# Revit family: 303_R14X_
name_source: partatom
category: Pipe Accessories
revit_build: Autodesk Revit 2018 (Build: 20170223_1515(x64)
units: mm (PartAtom-declared; Revit-internal decimal feet)

## family parameters
Always vertical = Yes
Cut with Voids When Loaded = No
Part Type = Valve - Breaks Into
Round Connector Dimension = Use Diameter
Shared = No
Work Plane-Based = No

## types (5) — shared parameters
CAT0 = Yes
CAT1 = No
Description = Angle lockshild valve
L2D_Min = 3048 mm
Manufacturer = Giacomini
QmdConnectorList = 301;D;302;D1
RC = No
URL = http://www.giacomini.com
Z1 = 2 mm  [stored 0.00656168 ft]
Z2 = 15 mm  [stored 0.0492126 ft]
magiPartTypeId = 303
magiProductFamilyId = R14X*
zero-valued in all types: MC_Default_elevation

## per-type parameters (varying)
- R14X032: B1=8 mm  [stored 0.0262467 ft]; B4=9 mm  [stored 0.0295276 ft]; CenSd_K1_6=10 mm  [stored 0.0328084 ft]; CenSd_W2_6=12 mm  [stored 0.0393701 ft]; D=10 mm; D1=10 mm; G1=8 mm  [stored 0.0262467 ft]; G3=10 mm  [stored 0.0328084 ft]; H3=9 mm  [stored 0.0295276 ft]; H3__ve=-9 mm; J=19 mm  [stored 0.062336 ft]; J1=5 mm  [stored 0.0164042 ft]; J3=7 mm  [stored 0.0229659 ft]; K1=11 mm  [stored 0.0360892 ft]; KH=8 mm  [stored 0.0262467 ft]; KH__ve=-8 mm  [stored -0.0262467 ft]; L=38 mm; L2=49 mm; L2D=38 mm; L3=7 mm  [stored 0.0229659 ft]; L4=7 mm  [stored 0.0229659 ft]; L4__ve=-7 mm; L5=3 mm  [stored 0.00984252 ft]; L8=10 mm  [stored 0.0328084 ft]; L8__ve=-10 mm  [stored -0.0328084 ft]; M1=15 mm  [stored 0.0492126 ft]; M12=11 mm  [stored 0.0360892 ft]; M3=17 mm  [stored 0.0557743 ft]; M3__ve=-17 mm  [stored -0.0557743 ft]; R1=8 mm  [stored 0.0262467 ft]; RC1=Yes; RC2=Yes; RC4=No; SW1=Yes; SW2=No; W1=11 mm  [stored 0.0360892 ft]; W2=14 mm  [stored 0.0459318 ft]; W2D=10 mm  [stored 0.0328084 ft]; W3=9 mm  [stored 0.0295276 ft]; X1=17 mm  [stored 0.0557743 ft]; X11=35 mm; X4=5 mm  [stored 0.0164042 ft]; Z4=11 mm  [stored 0.0360892 ft]
- R14X036: B1=17 mm  [stored 0.0557743 ft]; B4=21 mm  [stored 0.0688976 ft]; CenSd_K1_6=21 mm  [stored 0.0688976 ft]; CenSd_W2_6=23 mm; D=32 mm; D1=32 mm; G1=19 mm  [stored 0.062336 ft]; G3=21 mm  [stored 0.0688976 ft]; H3=18 mm; H3__ve=-18 mm; J=34 mm; J1=27 mm; J3=29 mm; K1=25 mm  [stored 0.082021 ft]; KH=14 mm  [stored 0.0459318 ft]; KH__ve=-14 mm; L=61 mm; L2=79 mm; L2D=60 mm; L3=13 mm; L4=13 mm; L4__ve=-13 mm; L5=6 mm  [stored 0.019685 ft]; L8=19 mm  [stored 0.062336 ft]; L8__ve=-19 mm  [stored -0.062336 ft]; M1=23 mm; M12=17 mm  [stored 0.0557743 ft]; M3=25 mm  [stored 0.082021 ft]; M3__ve=-25 mm; R1=19 mm  [stored 0.062336 ft]; RC1=No; RC2=No; RC4=Yes; SW1=No; SW2=Yes; W1=21 mm  [stored 0.0688976 ft]; W2=27 mm; W2D=32 mm; W3=19 mm  [stored 0.062336 ft]; X1=25 mm  [stored 0.082021 ft]; X11=54 mm; X4=9 mm  [stored 0.0295276 ft]; Z4=20 mm  [stored 0.0656168 ft]
- R14X035: B1=14 mm  [stored 0.0459318 ft]; B4=17 mm  [stored 0.0557743 ft]; CenSd_K1_6=17 mm  [stored 0.0557743 ft]; CenSd_W2_6=20 mm  [stored 0.0656168 ft]; D=25 mm; D1=25 mm; G1=15 mm  [stored 0.0492126 ft]; G3=17 mm  [stored 0.0557743 ft]; H3=16 mm  [stored 0.0524934 ft]; H3__ve=-16 mm; J=30 mm; J1=23 mm; J3=25 mm  [stored 0.082021 ft]; K1=20 mm  [stored 0.0656168 ft]; KH=12 mm  [stored 0.0393701 ft]; KH__ve=-12 mm; L=51 mm; L2=66 mm; L2D=51 mm; L3=10 mm  [stored 0.0328084 ft]; L4=10 mm  [stored 0.0328084 ft]; L4__ve=-10 mm  [stored -0.0328084 ft]; L5=5 mm  [stored 0.0164042 ft]; L8=15 mm  [stored 0.0492126 ft]; L8__ve=-15 mm  [stored -0.0492126 ft]; M1=20 mm  [stored 0.0656168 ft]; M12=14 mm  [stored 0.0459318 ft]; M3=22 mm; M3__ve=-22 mm; R1=16 mm  [stored 0.0524934 ft]; RC1=No; RC2=No; RC4=Yes; SW1=No; SW2=Yes; W1=18 mm; W2=23 mm; W2D=25 mm  [stored 0.082021 ft]; W3=16 mm  [stored 0.0524934 ft]; X1=22 mm; X11=46 mm; X4=8 mm  [stored 0.0262467 ft]; Z4=18 mm
- R14X034: B1=11 mm  [stored 0.0360892 ft]; B4=14 mm  [stored 0.0459318 ft]; CenSd_K1_6=14 mm  [stored 0.0459318 ft]; CenSd_W2_6=16 mm  [stored 0.0524934 ft]; D=20 mm; D1=20 mm; G1=13 mm; G3=15 mm  [stored 0.0492126 ft]; H3=12 mm  [stored 0.0393701 ft]; H3__ve=-12 mm; J=23 mm; J1=12 mm  [stored 0.0393701 ft]; J3=14 mm  [stored 0.0459318 ft]; K1=16 mm  [stored 0.0524934 ft]; KH=9 mm  [stored 0.0295276 ft]; KH__ve=-9 mm; L=45 mm; L2=58 mm; L2D=45 mm; L3=9 mm  [stored 0.0295276 ft]; L4=9 mm  [stored 0.0295276 ft]; L4__ve=-9 mm; L5=4 mm  [stored 0.0131234 ft]; L8=13 mm; L8__ve=-13 mm; M1=18 mm; M12=13 mm; M3=20 mm  [stored 0.0656168 ft]; M3__ve=-20 mm; R1=13 mm; RC1=No; RC2=No; RC4=Yes; SW1=No; SW2=Yes; W1=15 mm  [stored 0.0492126 ft]; W2=19 mm  [stored 0.062336 ft]; W2D=20 mm  [stored 0.0656168 ft]; W3=13 mm; X1=20 mm  [stored 0.0656168 ft]; X11=41 mm; X4=7 mm  [stored 0.0229659 ft]; Z4=14 mm  [stored 0.0459318 ft]
- R14X033: B1=9 mm  [stored 0.0295276 ft]; B4=11 mm  [stored 0.0360892 ft]; CenSd_K1_6=11 mm  [stored 0.0360892 ft]; CenSd_W2_6=13 mm; D=15 mm; D1=15 mm; G1=10 mm  [stored 0.0328084 ft]; G3=12 mm  [stored 0.0393701 ft]; H3=11 mm  [stored 0.0360892 ft]; H3__ve=-11 mm  [stored -0.0360892 ft]; J=21 mm  [stored 0.0688976 ft]; J1=7 mm  [stored 0.0229659 ft]; J3=9 mm  [stored 0.0295276 ft]; K1=13 mm; KH=8 mm  [stored 0.0262467 ft]; KH__ve=-8 mm  [stored -0.0262467 ft]; L=41 mm; L2=53 mm; L2D=41 mm; L3=8 mm  [stored 0.0262467 ft]; L4=8 mm  [stored 0.0262467 ft]; L4__ve=-8 mm  [stored -0.0262467 ft]; L5=4 mm  [stored 0.0131234 ft]; L8=12 mm  [stored 0.0393701 ft]; L8__ve=-12 mm; M1=15 mm  [stored 0.0492126 ft]; M12=11 mm  [stored 0.0360892 ft]; M3=17 mm  [stored 0.0557743 ft]; M3__ve=-17 mm  [stored -0.0557743 ft]; R1=11 mm  [stored 0.0360892 ft]; RC1=Yes; RC2=Yes; RC4=No; SW1=Yes; SW2=No; W1=12 mm  [stored 0.0393701 ft]; W2=15 mm  [stored 0.0492126 ft]; W2D=15 mm  [stored 0.0492126 ft]; W3=11 mm  [stored 0.0360892 ft]; X1=17 mm  [stored 0.0557743 ft]; X11=37 mm; X4=6 mm  [stored 0.019685 ft]; Z4=13 mm

note: column(s) folded — value = type name in every type: magiProductCode, magiProductId

note: [stored X ft] marks values corroborated as IEEE doubles in the binary element streams (Revit-internal decimal feet)

## geometry (parser evidence)
native form markers: Sweep x2
no freeform markers — native parametric forms only
